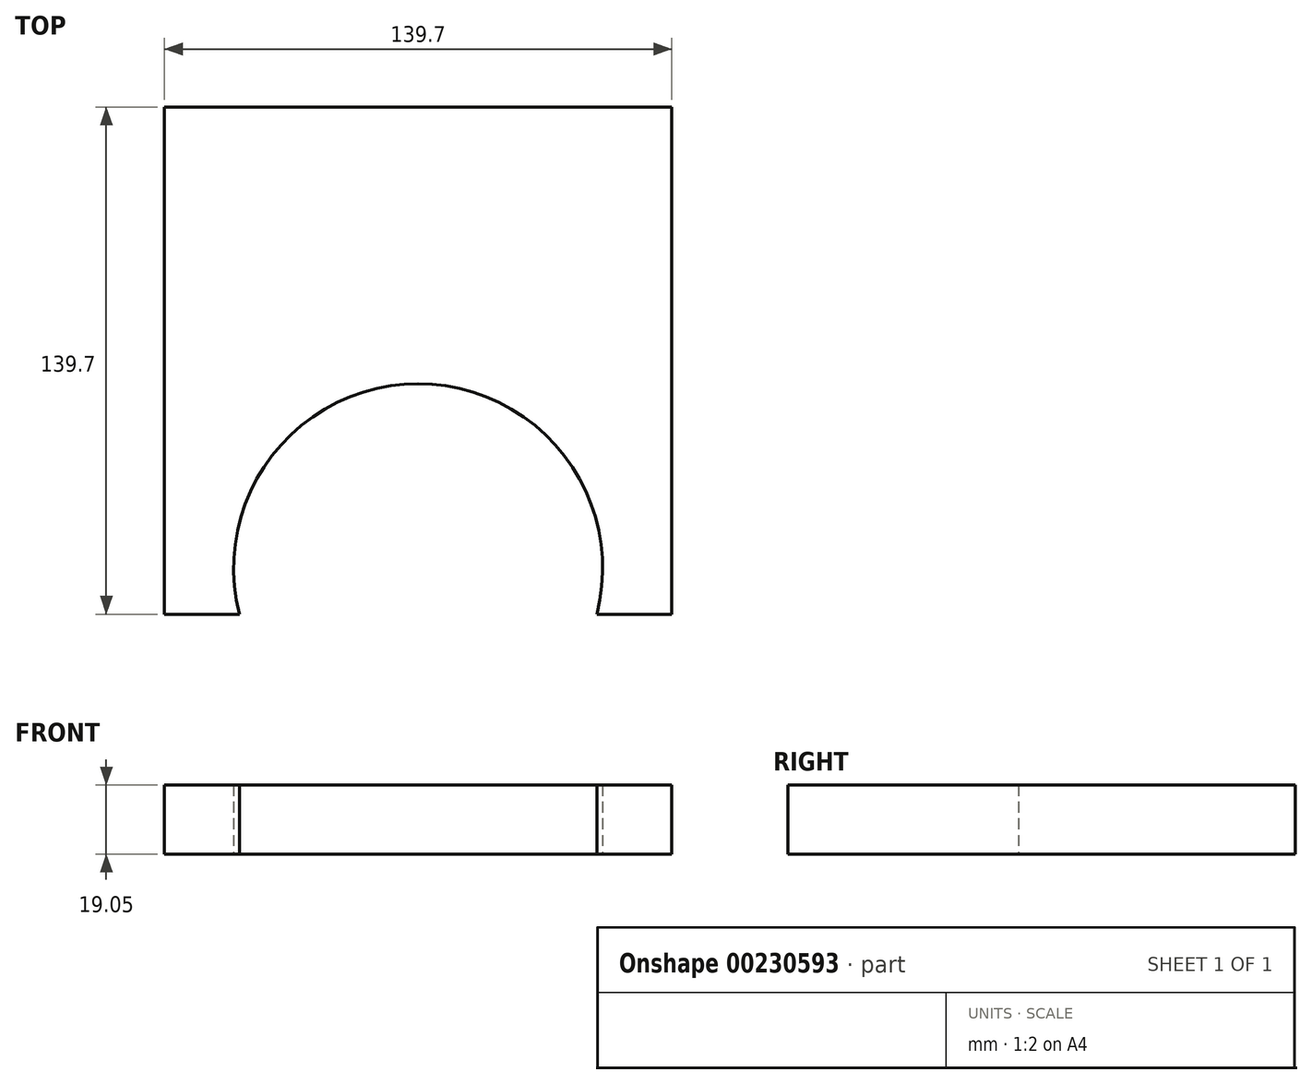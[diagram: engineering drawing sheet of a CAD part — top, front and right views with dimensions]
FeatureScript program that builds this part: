
annotation { "Feature Type Name" : "Feature", "Feature Type Description" : "" }
export const myFeature = defineFeature(function(context is Context, id is Id, definition is map)
    precondition{}
    {
        {
            var Q0;
            Q0=qCreatedBy(makeId("Top.planeOp"),FACE);
            var sketch = newSketch(context, id + "F0", { "sketchPlane" : qUnion([Q0])});
            skLineSegment(sketch, "E0.bottom", {"start": v(69.85, 69.85) * mm, "end": v(-69.85, 69.85) * mm});
            skLineSegment(sketch, "E0.top", {"start": v(69.85, -69.85) * mm, "end": v(49.19, -69.85) * mm});
            skLineSegment(sketch, "E0.left", {"start": v(69.85, 69.85) * mm, "end": v(69.85, -69.85) * mm});
            skLineSegment(sketch, "E0.right", {"start": v(-69.85, 69.85) * mm, "end": v(-69.85, -69.85) * mm});
            skPoint(sketch, "E0.middle", {"position": v(0, 0) * mm});
            skArc(sketch, "E1", {"start": v(49.19, -69.85) * mm, "mid": v(0, -6.35) * mm, "end": v(-49.19, -69.85) * mm});
            skLineSegment(sketch, "E2.trimOffspring", {"start": v(-49.19, -69.85) * mm, "end": v(-69.85, -69.85) * mm});
            skPoint(sketch, "E3.start.orphan", {"position": v(0, -69.85) * mm});
            skSolve(sketch);
        }
        {
            var Q0;
            Q0 = qSketchRegion(id + "F0", true);
            extrude(context, id + "F1", {"entities" : qUnion([Q0]), "depth" : 19.05 * mm});
        }
    });
